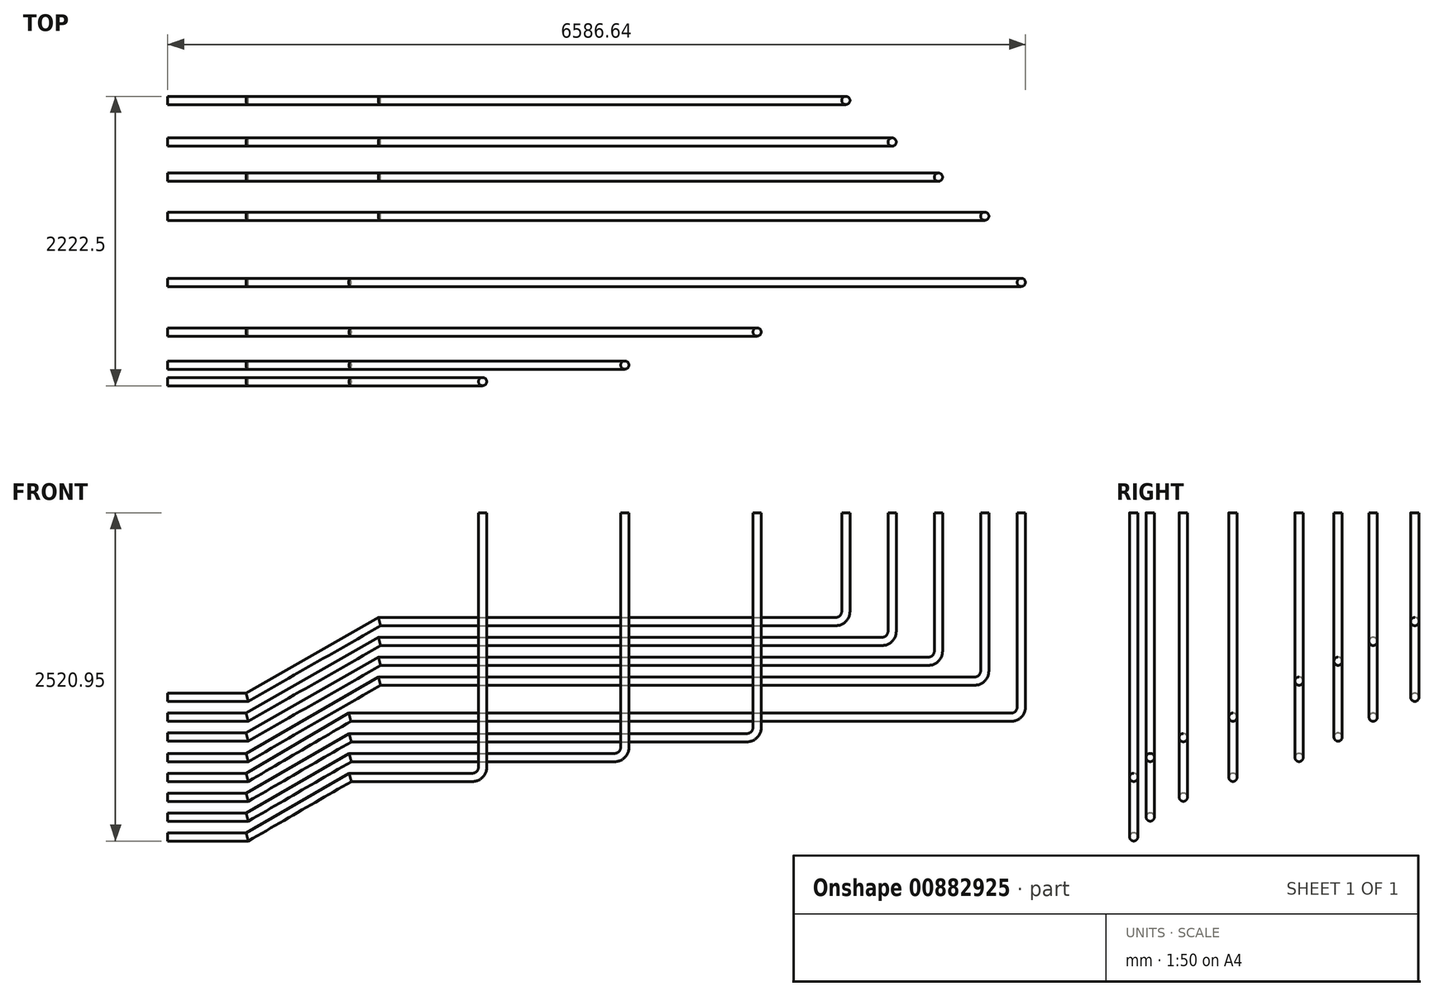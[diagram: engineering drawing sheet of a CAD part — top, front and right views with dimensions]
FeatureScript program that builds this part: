
annotation { "Feature Type Name" : "Feature", "Feature Type Description" : "" }
export const myFeature = defineFeature(function(context is Context, id is Id, definition is map)
    precondition{}
    {
        {
            var Q0;
            Q0=qCreatedBy(makeId("Front.planeOp"),FACE);
            var sketch = newSketch(context, id + "F0", { "sketchPlane" : qUnion([Q0])});
            skLineSegment(sketch, "E0", {"start": v(0, 0) * mm, "end": v(609.6, 0) * mm});
            skLineSegment(sketch, "E1", {"start": v(609.6, 0) * mm, "end": v(1401.5, 457.2) * mm});
            skLineSegment(sketch, "E2", {"start": v(1401.5, 457.2) * mm, "end": v(2341.3, 457.2) * mm});
            skLineSegment(sketch, "E3", {"start": v(2417.5, 533.4) * mm, "end": v(2417.5, 2489.2) * mm});
            skLineSegment(sketch, "E4", {"start": v(609.6, 0) * mm, "end": v(609.6, 924.03) * mm, "construction": true});
            skLineSegment(sketch, "E5", {"start": v(1401.5, 457.2) * mm, "end": v(1401.5, 1326) * mm, "construction": true});
            skLineSegment(sketch, "E6", {"start": v(2417.5, 2489.2) * mm, "end": v(6495.36, 2489.2) * mm, "construction": true});
            skLineSegment(sketch, "E7", {"start": v(0, 0) * mm, "end": v(0, 919.35) * mm, "construction": true});
            skPoint(sketch, "E8.visualSharp", {"position": v(2417.5, 457.2) * mm});
            skArc(sketch, "E8.filletArc", {"start": v(2341.3, 457.2) * mm, "mid": v(2395.18, 479.52) * mm, "end": v(2417.5, 533.4) * mm});
            skSolve(sketch);
        }
        {
            var Q0;
            Q0=qCreatedBy(makeId("Front.planeOp"),FACE);
            cPlane(context, id + "F1", {"entities" : qUnion([Q0]), "cplaneType" : CPlaneType.OFFSET, "offset" : 127 * mm, "oppositeDirection" : true, "width" : 152.4 * mm, "height" : 152.4 * mm});
        }
        {
            var Q0;
            Q0=qCreatedBy(id+"F1.planeOp",FACE);
            cPlane(context, id + "F2", {"entities" : qUnion([Q0]), "cplaneType" : CPlaneType.OFFSET, "offset" : 254 * mm, "oppositeDirection" : true, "width" : 152.4 * mm, "height" : 152.4 * mm});
        }
        {
            var Q0;
            Q0=qCreatedBy(id+"F2.planeOp",FACE);
            cPlane(context, id + "F3", {"entities" : qUnion([Q0]), "cplaneType" : CPlaneType.OFFSET, "offset" : 381 * mm, "oppositeDirection" : true, "width" : 152.4 * mm, "height" : 152.4 * mm});
        }
        {
            var Q0;
            Q0=qCreatedBy(id+"F1.planeOp",FACE);
            var sketch = newSketch(context, id + "F4", { "sketchPlane" : qUnion([Q0])});
            skLineSegment(sketch, "E9", {"start": v(0, 152.4) * mm, "end": v(609.6, 152.4) * mm});
            skLineSegment(sketch, "E10", {"start": v(609.6, 152.4) * mm, "end": v(1401.5, 609.6) * mm});
            skLineSegment(sketch, "E11", {"start": v(1401.5, 609.6) * mm, "end": v(3433.5, 609.6) * mm});
            skLineSegment(sketch, "E12", {"start": v(3509.7, 685.8) * mm, "end": v(3509.7, 2489.2) * mm});
            skPoint(sketch, "E13.visualSharp", {"position": v(3509.7, 609.6) * mm});
            skArc(sketch, "E13.filletArc", {"start": v(3433.5, 609.6) * mm, "mid": v(3487.38, 631.92) * mm, "end": v(3509.7, 685.8) * mm});
            skSolve(sketch);
        }
        {
            var Q0;
            Q0=qCreatedBy(id+"F2.planeOp",FACE);
            var sketch = newSketch(context, id + "F5", { "sketchPlane" : qUnion([Q0])});
            skLineSegment(sketch, "E14", {"start": v(0, 304.8) * mm, "end": v(609.6, 304.8) * mm});
            skLineSegment(sketch, "E15", {"start": v(609.6, 304.8) * mm, "end": v(1401.5, 762) * mm});
            skLineSegment(sketch, "E16", {"start": v(1401.5, 762) * mm, "end": v(4449.5, 762) * mm});
            skLineSegment(sketch, "E17", {"start": v(4525.7, 838.2) * mm, "end": v(4525.7, 2489.2) * mm});
            skPoint(sketch, "E18.visualSharp", {"position": v(4525.7, 762) * mm});
            skArc(sketch, "E18.filletArc", {"start": v(4449.5, 762) * mm, "mid": v(4503.38, 784.32) * mm, "end": v(4525.7, 838.2) * mm});
            skSolve(sketch);
        }
        {
            var Q0;
            Q0=qCreatedBy(id+"F3.planeOp",FACE);
            var sketch = newSketch(context, id + "F6", { "sketchPlane" : qUnion([Q0])});
            skLineSegment(sketch, "E19", {"start": v(0, 457.2) * mm, "end": v(609.6, 457.2) * mm});
            skLineSegment(sketch, "E20", {"start": v(609.6, 457.2) * mm, "end": v(1398.7, 919.21) * mm});
            skLineSegment(sketch, "E21", {"start": v(1398.7, 919.21) * mm, "end": v(6478.7, 919.21) * mm});
            skPoint(sketch, "E22.visualSharp", {"position": v(4786.6, 919.21) * mm});
            skArc(sketch, "E22.filletArc", {"start": v(6478.7, 919.21) * mm, "mid": v(6532.58, 941.53) * mm, "end": v(6554.9, 995.41) * mm});
            skLineSegment(sketch, "E23", {"start": v(6554.9, 995.41) * mm, "end": v(6554.9, 2489.2) * mm});
            skSolve(sketch);
        }
        {
            var Q0;
            Q0=qCreatedBy(makeId("Right.planeOp"),FACE);
            var sketch = newSketch(context, id + "F7", { "sketchPlane" : qUnion([Q0])});
            skPoint(sketch, "E24.0", {"position": v(127, 152.4) * mm});
            skPoint(sketch, "E25.0", {"position": v(381, 304.8) * mm});
            skPoint(sketch, "E26.0", {"position": v(762, 457.2) * mm});
            skCircle(sketch, "E27", {"center": v(0, 0) * mm, "radius": 31.75 * mm});
            skCircle(sketch, "E28", {"center": v(127, 152.4) * mm, "radius": 31.75 * mm});
            skCircle(sketch, "E29", {"center": v(381, 304.8) * mm, "radius": 31.75 * mm});
            skCircle(sketch, "E30", {"center": v(762, 457.2) * mm, "radius": 31.75 * mm});
            skSolve(sketch);
        }
        {
            var Q0;
            Q0=makeQuery(id+"F7.imprint","IMPRINT",FACE,{"disambiguationData":[TD([[makeQuery(id+"F7.imprint","IMPRINT",EDGE,{"derivedFrom":sQuery(id+"F7.wireOp",EDGE,"E27")}),1.0]])]});
            var Q1;
            Q1=sQuery(id+"F0.wireOp",EDGE,"E0");
            var Q2;
            Q2=sQuery(id+"F0.wireOp",EDGE,"E1");
            var Q3;
            Q3=sQuery(id+"F0.wireOp",EDGE,"E2");
            var Q4;
            Q4=sQuery(id+"F0.wireOp",EDGE,"E3");
            var Q5;
            Q5=sQuery(id+"F0.wireOp",EDGE,"E8.filletArc");
            sweep(context, id + "F8", {"profiles" : qUnion([Q0]), "path" : qUnion([Q1, Q2, Q3, Q4, Q5])});
        }
        {
            var Q0;
            Q0=makeQuery(id+"F7.imprint","IMPRINT",FACE,{"disambiguationData":[TD([[makeQuery(id+"F7.imprint","IMPRINT",EDGE,{"derivedFrom":sQuery(id+"F7.wireOp",EDGE,"E28")}),1.0]])]});
            var Q1;
            Q1=sQuery(id+"F4.wireOp",EDGE,"E9");
            var Q2;
            Q2=sQuery(id+"F4.wireOp",EDGE,"E10");
            var Q3;
            Q3=sQuery(id+"F4.wireOp",EDGE,"E11");
            var Q4;
            Q4=sQuery(id+"F4.wireOp",EDGE,"E12");
            var Q5;
            Q5=sQuery(id+"F4.wireOp",EDGE,"E13.filletArc");
            sweep(context, id + "F9", {"operationType" : NewBodyOperationType.ADD, "profiles" : qUnion([Q0]), "path" : qUnion([Q1, Q2, Q3, Q4, Q5])});
        }
        {
            var Q0;
            Q0=makeQuery(id+"F7.imprint","IMPRINT",FACE,{"disambiguationData":[TD([[makeQuery(id+"F7.imprint","IMPRINT",EDGE,{"derivedFrom":sQuery(id+"F7.wireOp",EDGE,"E29")}),1.0]])]});
            var Q1;
            Q1=sQuery(id+"F5.wireOp",EDGE,"E14");
            var Q2;
            Q2=sQuery(id+"F5.wireOp",EDGE,"E15");
            var Q3;
            Q3=sQuery(id+"F5.wireOp",EDGE,"E16");
            var Q4;
            Q4=sQuery(id+"F5.wireOp",EDGE,"E17");
            var Q5;
            Q5=sQuery(id+"F5.wireOp",EDGE,"E18.filletArc");
            sweep(context, id + "F10", {"operationType" : NewBodyOperationType.ADD, "profiles" : qUnion([Q0]), "path" : qUnion([Q1, Q2, Q3, Q4, Q5])});
        }
        {
            var Q0;
            Q0=makeQuery(id+"F7.imprint","IMPRINT",FACE,{"disambiguationData":[TD([[makeQuery(id+"F7.imprint","IMPRINT",EDGE,{"derivedFrom":sQuery(id+"F7.wireOp",EDGE,"E30")}),1.0]])]});
            var Q1;
            Q1=sQuery(id+"F6.wireOp",EDGE,"E19");
            var Q2;
            Q2=sQuery(id+"F6.wireOp",EDGE,"E20");
            var Q3;
            Q3=sQuery(id+"F6.wireOp",EDGE,"E21");
            var Q4;
            Q4=sQuery(id+"F6.wireOp",EDGE,"kmstWbAr-WwlY-FJDX-zBqN-sIfJ16JnLkCZ");
            var Q5;
            Q5=sQuery(id+"F6.wireOp",EDGE,"E22.filletArc");
            var Q6;
            Q6=sQuery(id+"F6.wireOp",EDGE,"E23");
            sweep(context, id + "F11", {"profiles" : qUnion([Q0]), "path" : qUnion([Q1, Q2, Q3, Q4, Q5, Q6])});
        }
        {
            var Q0;
            Q0=qCreatedBy(makeId("Front.planeOp"),FACE);
            cPlane(context, id + "F12", {"entities" : qUnion([Q0]), "cplaneType" : CPlaneType.OFFSET, "offset" : 1270 * mm, "oppositeDirection" : true, "width" : 152.4 * mm, "height" : 152.4 * mm});
        }
        {
            var Q0;
            Q0=qCreatedBy(id+"F12.planeOp",FACE);
            var sketch = newSketch(context, id + "F13", { "sketchPlane" : qUnion([Q0])});
            skPoint(sketch, "E31", {"position": v(0, 609.6) * mm});
            skLineSegment(sketch, "E32", {"start": v(0, 609.6) * mm, "end": v(609.6, 609.6) * mm});
            skLineSegment(sketch, "E33", {"start": v(609.6, 609.6) * mm, "end": v(1625.96, 1196.4) * mm});
            skLineSegment(sketch, "E34", {"start": v(1625.96, 1196.4) * mm, "end": v(6197.96, 1196.4) * mm});
            skLineSegment(sketch, "E35", {"start": v(6274.16, 1272.6) * mm, "end": v(6274.16, 2489.2) * mm});
            skPoint(sketch, "E36.visualSharp", {"position": v(6274.16, 1196.4) * mm});
            skArc(sketch, "E36.filletArc", {"start": v(6197.96, 1196.4) * mm, "mid": v(6251.84, 1218.71) * mm, "end": v(6274.16, 1272.6) * mm});
            skSolve(sketch);
        }
        {
            var Q0;
            Q0=qCreatedBy(makeId("Right.planeOp"),FACE);
            var sketch = newSketch(context, id + "F14", { "sketchPlane" : qUnion([Q0])});
            skCircle(sketch, "E37", {"center": v(1270, 609.6) * mm, "radius": 31.75 * mm});
            skSolve(sketch);
        }
        {
            var Q0;
            Q0=makeQuery(id+"F14.imprint","IMPRINT",FACE,{"disambiguationData":[TD([[makeQuery(id+"F14.imprint","IMPRINT",EDGE,{"derivedFrom":sQuery(id+"F14.wireOp",EDGE,"E37")}),1.0]])]});
            var Q1;
            Q1=sQuery(id+"F13.wireOp",EDGE,"E32");
            var Q2;
            Q2=sQuery(id+"F13.wireOp",EDGE,"E33");
            var Q3;
            Q3=sQuery(id+"F13.wireOp",EDGE,"E34");
            var Q4;
            Q4=sQuery(id+"F13.wireOp",EDGE,"E36.filletArc");
            var Q5;
            Q5=sQuery(id+"F13.wireOp",EDGE,"E35");
            sweep(context, id + "F15", {"profiles" : qUnion([Q0]), "path" : qUnion([Q1, Q2, Q3, Q4, Q5])});
        }
        {
            var Q0;
            Q0=qCreatedBy(id+"F12.planeOp",FACE);
            cPlane(context, id + "F16", {"entities" : qUnion([Q0]), "cplaneType" : CPlaneType.OFFSET, "offset" : 299.72 * mm, "oppositeDirection" : true, "width" : 152.4 * mm, "height" : 152.4 * mm});
        }
        {
            var Q0;
            Q0=qCreatedBy(id+"F16.planeOp",FACE);
            cPlane(context, id + "F17", {"entities" : qUnion([Q0]), "cplaneType" : CPlaneType.OFFSET, "offset" : 269.24 * mm, "oppositeDirection" : true, "width" : 152.4 * mm, "height" : 152.4 * mm});
        }
        {
            var Q0;
            Q0=qCreatedBy(id+"F17.planeOp",FACE);
            cPlane(context, id + "F18", {"entities" : qUnion([Q0]), "cplaneType" : CPlaneType.OFFSET, "offset" : 320.04 * mm, "oppositeDirection" : true, "width" : 152.4 * mm, "height" : 152.4 * mm});
        }
        {
            var Q0;
            Q0=qCreatedBy(id+"F16.planeOp",FACE);
            var sketch = newSketch(context, id + "F19", { "sketchPlane" : qUnion([Q0])});
            skLineSegment(sketch, "E38", {"start": v(0, 766.24) * mm, "end": v(609.6, 766.24) * mm});
            skLineSegment(sketch, "E39", {"start": v(609.6, 766.24) * mm, "end": v(1625.96, 1348.8) * mm});
            skLineSegment(sketch, "E40", {"start": v(1625.96, 1348.8) * mm, "end": v(5842.36, 1348.8) * mm});
            skPoint(sketch, "E41", {"position": v(1625.96, 1196.4) * mm});
            skLineSegment(sketch, "E42", {"start": v(1625.96, 1196.4) * mm, "end": v(1625.96, 2004.53) * mm, "construction": true});
            skLineSegment(sketch, "E43", {"start": v(5918.56, 1425) * mm, "end": v(5918.56, 2489.2) * mm});
            skPoint(sketch, "E44.visualSharp", {"position": v(5918.56, 1348.8) * mm});
            skArc(sketch, "E44.filletArc", {"start": v(5842.36, 1348.8) * mm, "mid": v(5896.24, 1371.11) * mm, "end": v(5918.56, 1425) * mm});
            skSolve(sketch);
        }
        {
            var Q0;
            Q0=qCreatedBy(id+"F17.planeOp",FACE);
            var sketch = newSketch(context, id + "F20", { "sketchPlane" : qUnion([Q0])});
            skLineSegment(sketch, "E45", {"start": v(0, 918.64) * mm, "end": v(609.6, 918.64) * mm});
            skLineSegment(sketch, "E46", {"start": v(609.6, 918.64) * mm, "end": v(1625.96, 1501.2) * mm});
            skLineSegment(sketch, "E47", {"start": v(1625.96, 1501.2) * mm, "end": v(5486.76, 1501.2) * mm});
            skLineSegment(sketch, "E48", {"start": v(5562.96, 1577.4) * mm, "end": v(5562.96, 2489.2) * mm});
            skPoint(sketch, "E49", {"position": v(1401.5, 1326) * mm});
            skLineSegment(sketch, "E50", {"start": v(1401.5, 1326) * mm, "end": v(1401.5, 2528.77) * mm, "construction": true});
            skLineSegment(sketch, "E51", {"start": v(0, 918.64) * mm, "end": v(0, 2488.75) * mm, "construction": true});
            skLineSegment(sketch, "E52", {"start": v(609.6, 918.64) * mm, "end": v(609.6, 2680.85) * mm, "construction": true});
            skPoint(sketch, "E53.visualSharp", {"position": v(5562.96, 1501.2) * mm});
            skArc(sketch, "E53.filletArc", {"start": v(5486.76, 1501.2) * mm, "mid": v(5540.64, 1523.51) * mm, "end": v(5562.96, 1577.4) * mm});
            skSolve(sketch);
        }
        {
            var Q0;
            Q0=qCreatedBy(id+"F18.planeOp",FACE);
            var sketch = newSketch(context, id + "F21", { "sketchPlane" : qUnion([Q0])});
            skLineSegment(sketch, "E54", {"start": v(0, 1071.75) * mm, "end": v(609.6, 1071.75) * mm});
            skLineSegment(sketch, "E55", {"start": v(609.6, 1071.75) * mm, "end": v(1625.96, 1653.6) * mm});
            skLineSegment(sketch, "E56", {"start": v(1625.96, 1653.6) * mm, "end": v(5131.16, 1653.6) * mm});
            skLineSegment(sketch, "E57", {"start": v(5207.36, 1729.8) * mm, "end": v(5207.36, 2489.2) * mm});
            skPoint(sketch, "E58.visualSharp", {"position": v(5207.36, 1653.6) * mm});
            skArc(sketch, "E58.filletArc", {"start": v(5131.16, 1653.6) * mm, "mid": v(5185.04, 1675.91) * mm, "end": v(5207.36, 1729.8) * mm});
            skSolve(sketch);
        }
        {
            var Q0;
            Q0=qCreatedBy(makeId("Right.planeOp"),FACE);
            var sketch = newSketch(context, id + "F22", { "sketchPlane" : qUnion([Q0])});
            skPoint(sketch, "E59", {"position": v(1569.72, 766.24) * mm});
            skPoint(sketch, "E60", {"position": v(1838.96, 918.64) * mm});
            skPoint(sketch, "E61", {"position": v(2159, 1071.75) * mm});
            skCircle(sketch, "E62", {"center": v(2159, 1071.75) * mm, "radius": 31.75 * mm});
            skCircle(sketch, "E63", {"center": v(1838.96, 918.64) * mm, "radius": 31.75 * mm});
            skCircle(sketch, "E64", {"center": v(1569.72, 766.24) * mm, "radius": 31.75 * mm});
            skSolve(sketch);
        }
        {
            var Q0;
            Q0=makeQuery(id+"F22.imprint","IMPRINT",FACE,{"disambiguationData":[TD([[makeQuery(id+"F22.imprint","IMPRINT",EDGE,{"derivedFrom":sQuery(id+"F22.wireOp",EDGE,"E64")}),1.0]])]});
            var Q1;
            Q1=sQuery(id+"F19.wireOp",EDGE,"E38");
            var Q2;
            Q2=sQuery(id+"F19.wireOp",EDGE,"E39");
            var Q3;
            Q3=sQuery(id+"F19.wireOp",EDGE,"E40");
            var Q4;
            Q4=sQuery(id+"F19.wireOp",EDGE,"E44.filletArc");
            var Q5;
            Q5=sQuery(id+"F19.wireOp",EDGE,"E43");
            sweep(context, id + "F23", {"profiles" : qUnion([Q0]), "path" : qUnion([Q1, Q2, Q3, Q4, Q5])});
        }
        {
            var Q0;
            Q0=makeQuery(id+"F22.imprint","IMPRINT",FACE,{"disambiguationData":[TD([[makeQuery(id+"F22.imprint","IMPRINT",EDGE,{"derivedFrom":sQuery(id+"F22.wireOp",EDGE,"E63")}),1.0]])]});
            var Q1;
            Q1=sQuery(id+"F20.wireOp",EDGE,"E45");
            var Q2;
            Q2=sQuery(id+"F20.wireOp",EDGE,"E47");
            var Q3;
            Q3=sQuery(id+"F20.wireOp",EDGE,"E46");
            var Q4;
            Q4=sQuery(id+"F20.wireOp",EDGE,"E53.filletArc");
            var Q5;
            Q5=sQuery(id+"F20.wireOp",EDGE,"E48");
            sweep(context, id + "F24", {"profiles" : qUnion([Q0]), "path" : qUnion([Q1, Q2, Q3, Q4, Q5])});
        }
        {
            var Q0;
            Q0=makeQuery(id+"F22.imprint","IMPRINT",FACE,{"disambiguationData":[TD([[makeQuery(id+"F22.imprint","IMPRINT",EDGE,{"derivedFrom":sQuery(id+"F22.wireOp",EDGE,"E62")}),1.0]])]});
            var Q1;
            Q1=sQuery(id+"F21.wireOp",EDGE,"E54");
            var Q2;
            Q2=sQuery(id+"F21.wireOp",EDGE,"E55");
            var Q3;
            Q3=sQuery(id+"F21.wireOp",EDGE,"E56");
            var Q4;
            Q4=sQuery(id+"F21.wireOp",EDGE,"E58.filletArc");
            var Q5;
            Q5=sQuery(id+"F21.wireOp",EDGE,"E57");
            sweep(context, id + "F25", {"profiles" : qUnion([Q0]), "path" : qUnion([Q1, Q2, Q3, Q4, Q5])});
        }
    });
